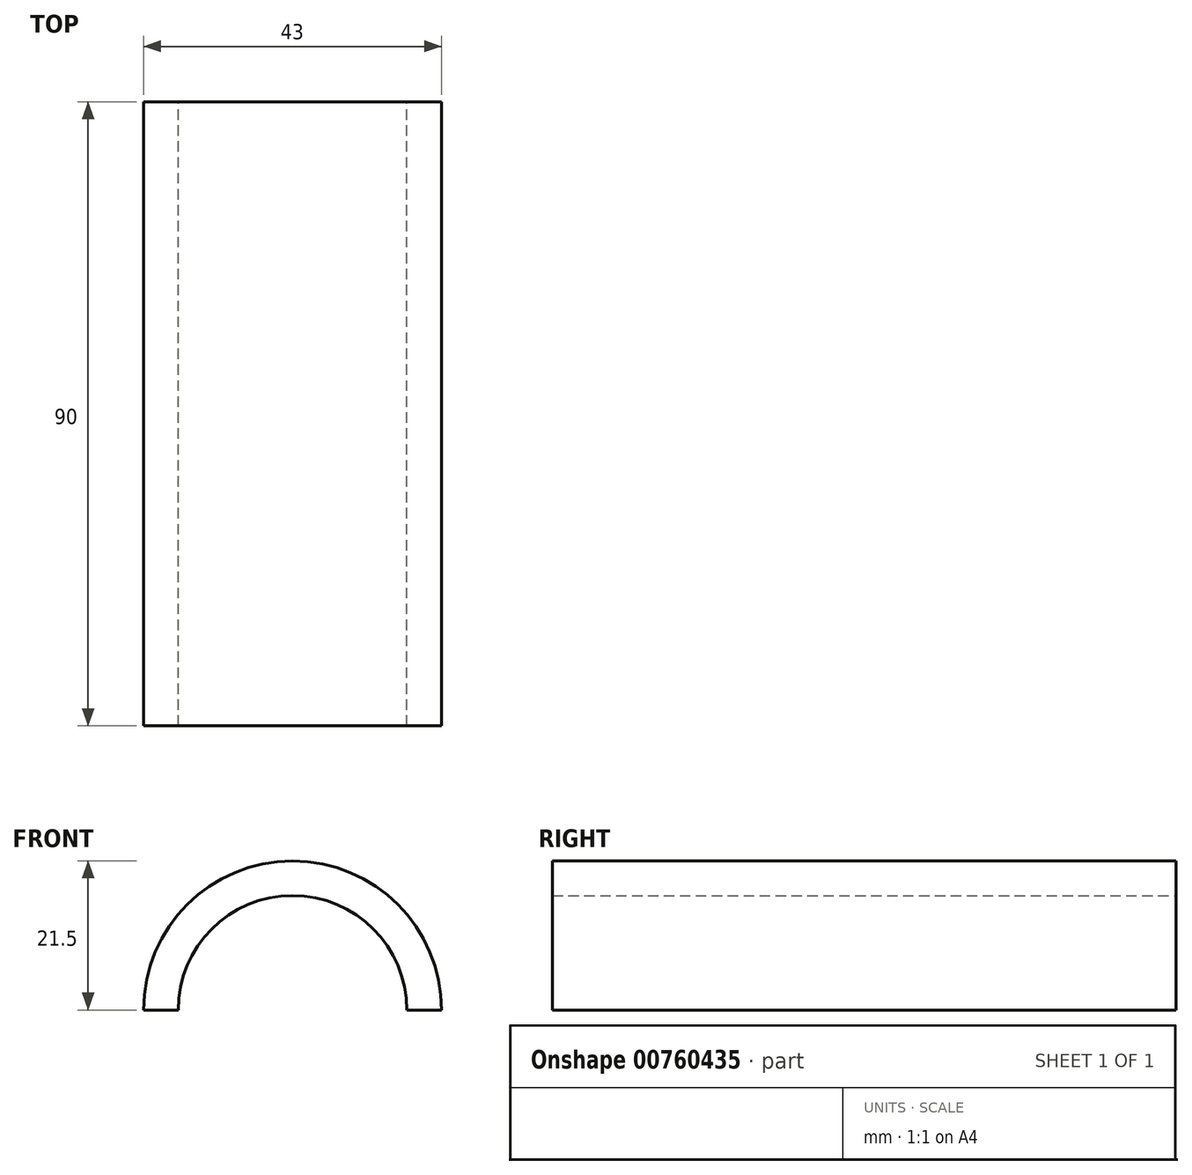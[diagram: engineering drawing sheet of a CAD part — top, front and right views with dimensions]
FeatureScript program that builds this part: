
annotation { "Feature Type Name" : "Feature", "Feature Type Description" : "" }
export const myFeature = defineFeature(function(context is Context, id is Id, definition is map)
    precondition{}
    {
        {
            var Q0;
            Q0=qCreatedBy(makeId("Front.planeOp"),FACE);
            var sketch = newSketch(context, id + "F0", { "sketchPlane" : qUnion([Q0])});
            skArc(sketch, "E0", {"start": v(33, 0) * mm, "mid": v(16.5, 16.5) * mm, "end": v(0, 0) * mm});
            skArc(sketch, "E1.0", {"start": v(38, 0) * mm, "mid": v(16.5, 21.5) * mm, "end": v(-5, 0) * mm});
            skLineSegment(sketch, "E2", {"start": v(-5, 0) * mm, "end": v(0, 0) * mm});
            skLineSegment(sketch, "E3", {"start": v(33, 0) * mm, "end": v(38, 0) * mm});
            skSolve(sketch);
        }
        {
            var Q0;
            Q0=makeQuery(id+"F0.imprint","IMPRINT",FACE,{"disambiguationData":[TD([[makeQuery(id+"F0.imprint","IMPRINT",EDGE,{"derivedFrom":sQuery(id+"F0.wireOp",EDGE,"E0")}),-1.0]])]});
            extrude(context, id + "F1", {"entities" : qUnion([Q0]), "depth" : 90 * mm, "offsetDistance" : 25 * mm});
        }
        {
            var Q0;
            Q0=qCreatedBy(makeId("Top.planeOp"),FACE);
            cPlane(context, id + "F2", {"entities" : qUnion([Q0]), "cplaneType" : CPlaneType.OFFSET, "offset" : 21.5 * mm, "width" : 150 * mm, "height" : 150 * mm});
        }
    });
